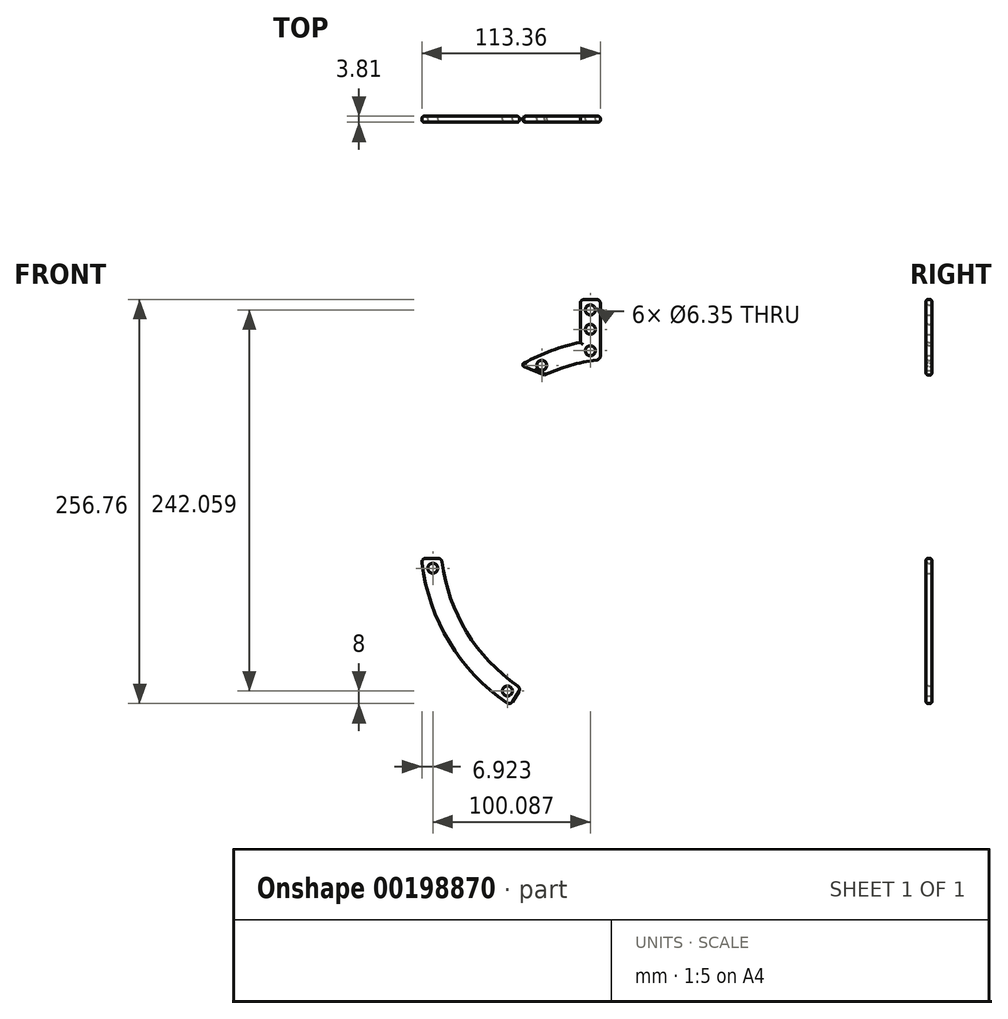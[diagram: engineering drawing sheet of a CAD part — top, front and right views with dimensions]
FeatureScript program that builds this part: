
annotation { "Feature Type Name" : "Feature", "Feature Type Description" : "" }
export const myFeature = defineFeature(function(context is Context, id is Id, definition is map)
    precondition{}
    {
        {
            var Q0;
            Q0=qCreatedBy(makeId("Front.planeOp"),FACE);
            var sketch = newSketch(context, id + "F0", { "sketchPlane" : qUnion([Q0])});
            skArc(sketch, "E0", {"start": v(-113.6, -12.7) * mm, "mid": v(-97.55, -59.57) * mm, "end": v(-63.18, -95.25) * mm});
            skArc(sketch, "E1", {"start": v(-126.36, -12.7) * mm, "mid": v(-108.66, -65.74) * mm, "end": v(-69.89, -106.04) * mm});
            skLineSegment(sketch, "E2.trimOffspring", {"start": v(-113.6, -12.7) * mm, "end": v(-126.36, -12.7) * mm});
            skArc(sketch, "E3.trimOffspring", {"start": v(-12.7, 113.6) * mm, "mid": v(-30.89, 110.05) * mm, "end": v(-48.26, 103.61) * mm});
            skLineSegment(sketch, "E4.trimOffspring", {"start": v(-12.7, 113.6) * mm, "end": v(-12.7, 151.76) * mm});
            skCircle(sketch, "E5", {"center": v(-119.14, -19.05) * mm, "radius": 3.18 * mm});
            skCircle(sketch, "E6", {"center": v(-19.05, 119.14) * mm, "radius": 3.18 * mm});
            skPoint(sketch, "E7.centerSnap0", {"position": v(19.05, 119.98) * mm});
            skPoint(sketch, "E8.centerSnap0", {"position": v(119.98, 19.05) * mm});
            skPoint(sketch, "E9.centerSnap0", {"position": v(119.98, -19.05) * mm});
            skPoint(sketch, "E10.0.start.orphan", {"position": v(113.6, -19.05) * mm});
            skPoint(sketch, "E11.trimOffspring.end.orphan", {"position": v(126.36, -19.05) * mm});
            skPoint(sketch, "E12.0.start.orphan", {"position": v(113.6, 19.05) * mm});
            skPoint(sketch, "E13.trimOffspring.end.orphan", {"position": v(126.36, 19.05) * mm});
            skPoint(sketch, "E14.0.start.orphan", {"position": v(19.05, 113.6) * mm});
            skPoint(sketch, "E15.trimOffspring.end.orphan", {"position": v(19.05, 126.36) * mm});
            skLineSegment(sketch, "E16.0", {"start": v(-25.4, 151.76) * mm, "end": v(-12.7, 151.76) * mm});
            skCircle(sketch, "E17", {"center": v(-19.05, 145.06) * mm, "radius": 3.18 * mm});
            skCircle(sketch, "E18", {"center": v(-19.05, 132.71) * mm, "radius": 3.18 * mm});
            skLineSegment(sketch, "E19.trimOffspring", {"start": v(-19.05, 145.06) * mm, "end": v(-19.05, 145.41) * mm});
            skPoint(sketch, "E20.orphan", {"position": v(25.4, 132.71) * mm});
            skPoint(sketch, "E21.orphan", {"position": v(25.4, 158.11) * mm});
            skPoint(sketch, "E22.orphan", {"position": v(19.05, 164.46) * mm});
            skPoint(sketch, "E23.center.orphan", {"position": v(19.05, 158.11) * mm});
            skArc(sketch, "E24.converted", {"start": v(-25.4, 124.43) * mm, "mid": v(-45.03, 118.75) * mm, "end": v(-63.5, 109.99) * mm});
            skLineSegment(sketch, "E25", {"start": v(-63.5, 109.99) * mm, "end": v(-48.26, 103.61) * mm});
            skPoint(sketch, "E26.center.orphan", {"position": v(19.05, 145.41) * mm});
            skPoint(sketch, "E27.center.orphan", {"position": v(19.05, 132.71) * mm});
            skPoint(sketch, "E7.center.orphan", {"position": v(19.05, 119.14) * mm});
            skPoint(sketch, "E8.center.orphan", {"position": v(119.14, 19.05) * mm});
            skPoint(sketch, "E9.center.orphan", {"position": v(119.14, -19.05) * mm});
            skLineSegment(sketch, "E28", {"start": v(-63.18, -95.25) * mm, "end": v(-69.89, -106.04) * mm});
            skCircle(sketch, "E29", {"center": v(-49.89, 109.85) * mm, "radius": 3.18 * mm});
            skLineSegment(sketch, "E30", {"start": v(-25.4, 151.76) * mm, "end": v(-25.4, 124.43) * mm});
            skCircle(sketch, "E31", {"center": v(-71.75, -97) * mm, "radius": 3.18 * mm});
            skSolve(sketch);
        }
        {
            var Q0;
            Q0=makeQuery(id+"F0.imprint","IMPRINT",FACE,{"disambiguationData":[TD([[makeQuery(id+"F0.imprint","IMPRINT",EDGE,{"derivedFrom":sQuery(id+"F0.wireOp",EDGE,"E3.trimOffspring")}),-1.0]])]});
            var Q1;
            Q1=makeQuery(id+"F0.imprint","IMPRINT",FACE,{"disambiguationData":[TD([[makeQuery(id+"F0.imprint","IMPRINT",EDGE,{"derivedFrom":sQuery(id+"F0.wireOp",EDGE,"E0")}),-1.0]])]});
            extrude(context, id + "F4", {"entities" : qUnion([Q0, Q1]), "depth" : 3.8 * mm});
        }
        {
            var Q0;
            Q0=makeQuery(id+"F4.opExtrude","CAP_FACE",FACE,{"disambiguationData":[OSD([sQuery(id+"F0.wireOp",EDGE,"E0"),sQuery(id+"F0.wireOp",EDGE,"E2.trimOffspring"),sQuery(id+"F0.wireOp",EDGE,"E5"),sQuery(id+"F0.wireOp",EDGE,"E1"),sQuery(id+"F0.wireOp",EDGE,"E28"),sQuery(id+"F0.wireOp",EDGE,"E31")])],"isStart":false});
            var Q1;
            Q1=makeQuery(id+"F4.opExtrude","CAP_FACE",FACE,{"disambiguationData":[OSD([sQuery(id+"F0.wireOp",EDGE,"E3.trimOffspring"),sQuery(id+"F0.wireOp",EDGE,"E4.trimOffspring"),sQuery(id+"F0.wireOp",EDGE,"E6"),sQuery(id+"F0.wireOp",EDGE,"E16.0"),sQuery(id+"F0.wireOp",EDGE,"E17"),sQuery(id+"F0.wireOp",EDGE,"E18"),sQuery(id+"F0.wireOp",EDGE,"E24.converted"),sQuery(id+"F0.wireOp",EDGE,"E25"),sQuery(id+"F0.wireOp",EDGE,"E29"),sQuery(id+"F0.wireOp",EDGE,"E30")])],"isStart":true});
            var Q2;
            Q2=makeQuery(id+"F4.opExtrude","CAP_FACE",FACE,{"disambiguationData":[OSD([sQuery(id+"F0.wireOp",EDGE,"E3.trimOffspring"),sQuery(id+"F0.wireOp",EDGE,"E4.trimOffspring"),sQuery(id+"F0.wireOp",EDGE,"E6"),sQuery(id+"F0.wireOp",EDGE,"E16.0"),sQuery(id+"F0.wireOp",EDGE,"E17"),sQuery(id+"F0.wireOp",EDGE,"E18"),sQuery(id+"F0.wireOp",EDGE,"E24.converted"),sQuery(id+"F0.wireOp",EDGE,"E25"),sQuery(id+"F0.wireOp",EDGE,"E29"),sQuery(id+"F0.wireOp",EDGE,"E30")])],"isStart":false});
            var Q3;
            Q3=makeQuery(id+"F4.opExtrude","CAP_FACE",FACE,{"disambiguationData":[OSD([sQuery(id+"F0.wireOp",EDGE,"E0"),sQuery(id+"F0.wireOp",EDGE,"E2.trimOffspring"),sQuery(id+"F0.wireOp",EDGE,"E5"),sQuery(id+"F0.wireOp",EDGE,"E1"),sQuery(id+"F0.wireOp",EDGE,"E28"),sQuery(id+"F0.wireOp",EDGE,"E31")])],"isStart":true});
            fillet(context, id + "F5", {"entities" : qUnion([Q0, Q1, Q2, Q3]), "radius" : 1.52 * mm, "tangentPropagation" : true, "allowEdgeOverflow" : false});
        }
        {
            var Q0;
            Q0=makeQuery(id+"F4.opExtrude","SWEPT_EDGE",EDGE,{"disambiguationData":[OSD([sQuery(id+"F0.wireOp",EDGE,"E2.trimOffspring"),sQuery(id+"F0.wireOp",EDGE,"E1")])]});
            var Q1;
            Q1=makeQuery(id+"F4.opExtrude","SWEPT_EDGE",EDGE,{"disambiguationData":[OSD([sQuery(id+"F0.wireOp",EDGE,"E1"),sQuery(id+"F0.wireOp",EDGE,"E28")])]});
            var Q2;
            Q2=makeQuery(id+"F4.opExtrude","SWEPT_EDGE",EDGE,{"disambiguationData":[OSD([sQuery(id+"F0.wireOp",EDGE,"E0"),sQuery(id+"F0.wireOp",EDGE,"E28")])]});
            fillet(context, id + "F1", {"entities" : qUnion([Q0, Q1, Q2]), "radius" : 2.54 * mm, "tangentPropagation" : true, "allowEdgeOverflow" : false});
        }
        {
            var Q0;
            Q0=makeQuery(id+"F4.opExtrude","SWEPT_EDGE",EDGE,{"disambiguationData":[OSD([sQuery(id+"F0.wireOp",EDGE,"E0"),sQuery(id+"F0.wireOp",EDGE,"E2.trimOffspring")])]});
            var Q1;
            Q1=makeQuery(id+"F4.opExtrude","SWEPT_EDGE",EDGE,{"disambiguationData":[OSD([sQuery(id+"F0.wireOp",EDGE,"E3.trimOffspring"),sQuery(id+"F0.wireOp",EDGE,"E4.trimOffspring")])]});
            var Q2;
            Q2=makeQuery(id+"F4.opExtrude","SWEPT_EDGE",EDGE,{"disambiguationData":[OSD([sQuery(id+"F0.wireOp",EDGE,"E4.trimOffspring"),sQuery(id+"F0.wireOp",EDGE,"E16.0")])]});
            var Q3;
            Q3=makeQuery(id+"F4.opExtrude","SWEPT_EDGE",EDGE,{"disambiguationData":[OSD([sQuery(id+"F0.wireOp",EDGE,"E16.0"),sQuery(id+"F0.wireOp",EDGE,"E30")])]});
            fillet(context, id + "F2", {"entities" : qUnion([Q0, Q1, Q2, Q3]), "radius" : 2.54 * mm, "tangentPropagation" : true, "allowEdgeOverflow" : false});
        }
        {
            var Q0;
            Q0=makeQuery(id+"F4.opExtrude","SWEPT_EDGE",EDGE,{"disambiguationData":[OSD([sQuery(id+"F0.wireOp",EDGE,"E24.converted"),sQuery(id+"F0.wireOp",EDGE,"E25")])]});
            fillet(context, id + "F3", {"entities" : qUnion([Q0]), "radius" : 1.27 * mm, "tangentPropagation" : true, "allowEdgeOverflow" : false});
        }
    });
